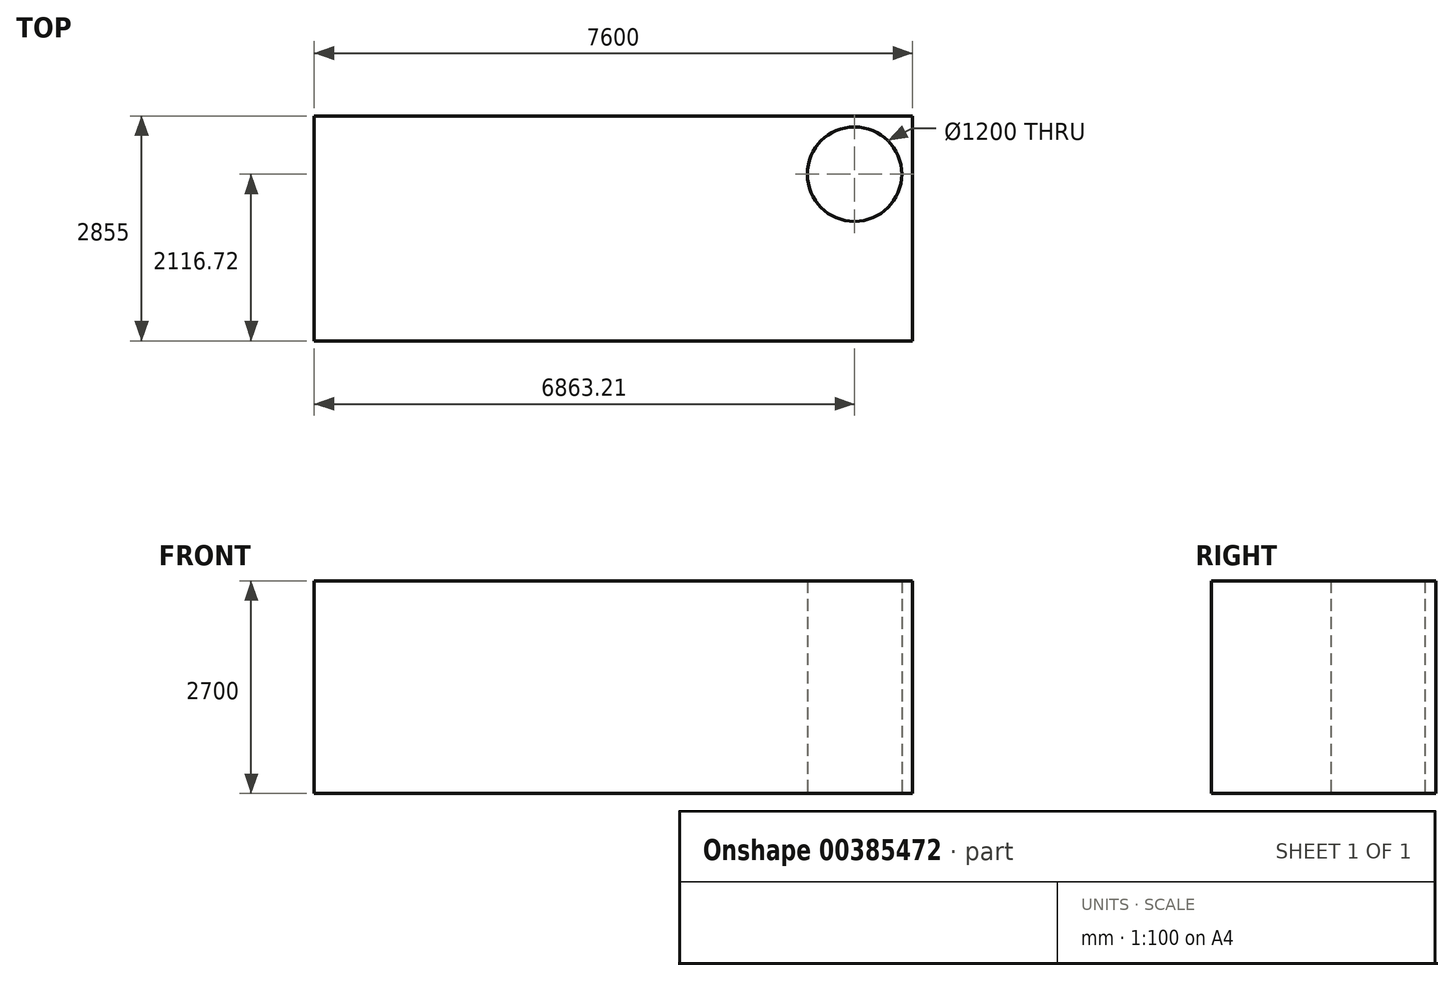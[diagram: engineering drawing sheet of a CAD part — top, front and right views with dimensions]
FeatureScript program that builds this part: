
annotation { "Feature Type Name" : "Feature", "Feature Type Description" : "" }
export const myFeature = defineFeature(function(context is Context, id is Id, definition is map)
    precondition{}
    {
        {
            var Q0;
            Q0=qCreatedBy(makeId("Top.planeOp"),FACE);
            var sketch = newSketch(context, id + "F0", { "sketchPlane" : qUnion([Q0])});
            skLineSegment(sketch, "E0.bottom", {"start": v(-3800, -1427.5) * mm, "end": v(3800, -1427.5) * mm});
            skLineSegment(sketch, "E0.top", {"start": v(-3800, 1427.5) * mm, "end": v(3800, 1427.5) * mm});
            skLineSegment(sketch, "E0.left", {"start": v(-3800, -1427.5) * mm, "end": v(-3800, 1427.5) * mm});
            skLineSegment(sketch, "E0.right", {"start": v(3800, -1427.5) * mm, "end": v(3800, 1427.5) * mm});
            skPoint(sketch, "E0.middle", {"position": v(0, 0) * mm});
            skSolve(sketch);
        }
        {
            var Q0;
            Q0=makeQuery(id+"F0.imprint","IMPRINT",FACE,{"disambiguationData":[TD([[makeQuery(id+"F0.imprint","IMPRINT",EDGE,{"derivedFrom":sQuery(id+"F0.wireOp",EDGE,"E0.bottom")}),1.0]])]});
            var sketch = newSketch(context, id + "F1", { "sketchPlane" : qUnion([Q0])});
            skCircle(sketch, "E1", {"center": v(3063.21, 689.22) * mm, "radius": 600 * mm});
            skSolve(sketch);
        }
        {
            var Q0;
            Q0=makeQuery(id+"F1.imprint","IMPRINT",FACE,{"disambiguationData":[TD([[makeQuery(id+"F1.imprint","IMPRINT",EDGE,{"derivedFrom":sQuery(id+"F1.wireOp",EDGE,"E1")}),-1.0]])]});
            extrude(context, id + "F2", {"entities" : qUnion([Q0]), "depth" : 2700 * mm});
        }
    });
